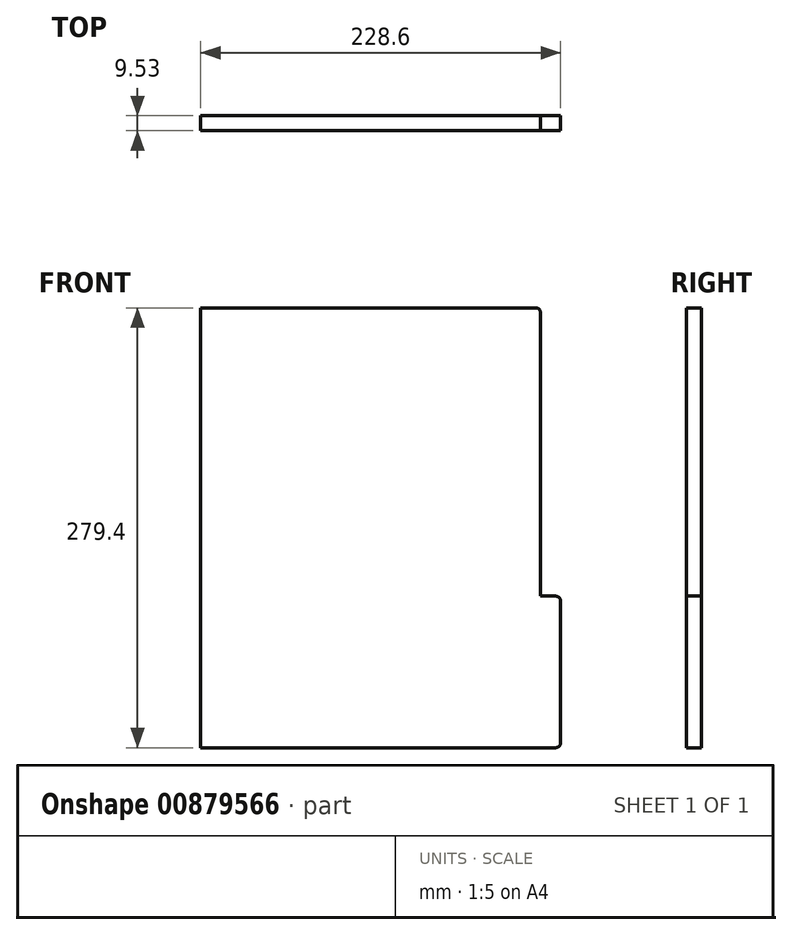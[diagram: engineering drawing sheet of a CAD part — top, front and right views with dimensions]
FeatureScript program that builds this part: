
annotation { "Feature Type Name" : "Feature", "Feature Type Description" : "" }
export const myFeature = defineFeature(function(context is Context, id is Id, definition is map)
    precondition{}
    {
        {
            var Q0;
            Q0=qCreatedBy(makeId("Front.planeOp"),FACE);
            var sketch = newSketch(context, id + "F0", { "sketchPlane" : qUnion([Q0])});
            skLineSegment(sketch, "E0.bottom", {"start": v(107.95, 139.7) * mm, "end": v(-107.95, 139.7) * mm});
            skLineSegment(sketch, "E0.top", {"start": v(107.95, -139.7) * mm, "end": v(-107.95, -139.7) * mm});
            skLineSegment(sketch, "E0.left", {"start": v(107.95, 139.7) * mm, "end": v(107.95, -139.7) * mm});
            skLineSegment(sketch, "E0.right", {"start": v(-107.95, 139.7) * mm, "end": v(-107.95, -139.7) * mm});
            skPoint(sketch, "E0.middle", {"position": v(0, 0) * mm});
            skSolve(sketch);
        }
        {
            var Q0;
            Q0 = qSketchRegion(id + "F0", true);
            extrude(context, id + "F1", {"entities" : qUnion([Q0]), "depth" : 9.52 * mm, "offsetDistance" : 25.4 * mm});
        }
        {
            var Q0;
            Q0=qCreatedBy(makeId("Front.planeOp"),FACE);
            var sketch = newSketch(context, id + "F2", { "sketchPlane" : qUnion([Q0])});
            skLineSegment(sketch, "E1.bottom", {"start": v(107.95, -139.7) * mm, "end": v(120.65, -139.7) * mm});
            skLineSegment(sketch, "E1.top", {"start": v(107.95, -43.4) * mm, "end": v(120.65, -43.4) * mm});
            skLineSegment(sketch, "E1.left", {"start": v(107.95, -139.7) * mm, "end": v(107.95, -43.4) * mm});
            skLineSegment(sketch, "E1.right", {"start": v(120.65, -139.7) * mm, "end": v(120.65, -43.4) * mm});
            skSolve(sketch);
        }
        {
            var Q0;
            Q0 = qSketchRegion(id + "F2", true);
            var Q1;
            Q1=makeQuery(id+"F1.opExtrude","CAP_FACE",FACE,{"disambiguationData":[OSD([sQuery(id+"F0.wireOp",EDGE,"E0.bottom"),sQuery(id+"F0.wireOp",EDGE,"E0.top"),sQuery(id+"F0.wireOp",EDGE,"E0.left"),sQuery(id+"F0.wireOp",EDGE,"E0.right")])],"isStart":false});
            extrude(context, id + "F3", {"entities" : qUnion([Q0]), "operationType" : NewBodyOperationType.ADD, "endBound" : BoundingType.UP_TO_SURFACE, "depth" : 25.4 * mm, "endBoundEntityFace" : qUnion([Q1]), "offsetDistance" : 25.4 * mm});
        }
        {
            var Q0;
            Q0=makeQuery(id+"F1.opExtrude","SWEPT_EDGE",EDGE,{"disambiguationData":[OSD([sQuery(id+"F0.wireOp",EDGE,"E0.bottom"),sQuery(id+"F0.wireOp",EDGE,"E0.left")])]});
            var Q1;
            Q1=makeQuery(id+"F3.opExtrude","SWEPT_EDGE",EDGE,{"disambiguationData":[OSD([sQuery(id+"F2.wireOp",EDGE,"E1.top"),sQuery(id+"F2.wireOp",EDGE,"E1.left")])]});
            var Q2;
            Q2=makeQuery(id+"F3.opExtrude","SWEPT_EDGE",EDGE,{"disambiguationData":[OSD([sQuery(id+"F2.wireOp",EDGE,"E1.top"),sQuery(id+"F2.wireOp",EDGE,"E1.right")])]});
            var Q3;
            Q3=makeQuery(id+"F3.opExtrude","SWEPT_EDGE",EDGE,{"disambiguationData":[OSD([sQuery(id+"F2.wireOp",EDGE,"E1.bottom"),sQuery(id+"F2.wireOp",EDGE,"E1.right")])]});
            var Q4;
            Q4=makeQuery(id+"F3.opExtrude","SWEPT_EDGE",EDGE,{"disambiguationData":[OSD([sQuery(id+"F2.wireOp",EDGE,"E1.bottom"),sQuery(id+"F2.wireOp",EDGE,"E1.left")])]});
            var Q5;
            Q5=makeQuery(id+"F1.opExtrude","SWEPT_EDGE",EDGE,{"disambiguationData":[OSD([sQuery(id+"F0.wireOp",EDGE,"E0.top"),sQuery(id+"F0.wireOp",EDGE,"E0.left")])]});
            fillet(context, id + "F4", {"entities" : qUnion([Q0, Q1, Q2, Q3, Q4, Q5]), "radius" : 3.17 * mm, "tangentPropagation" : true, "allowEdgeOverflow" : false});
        }
    });
